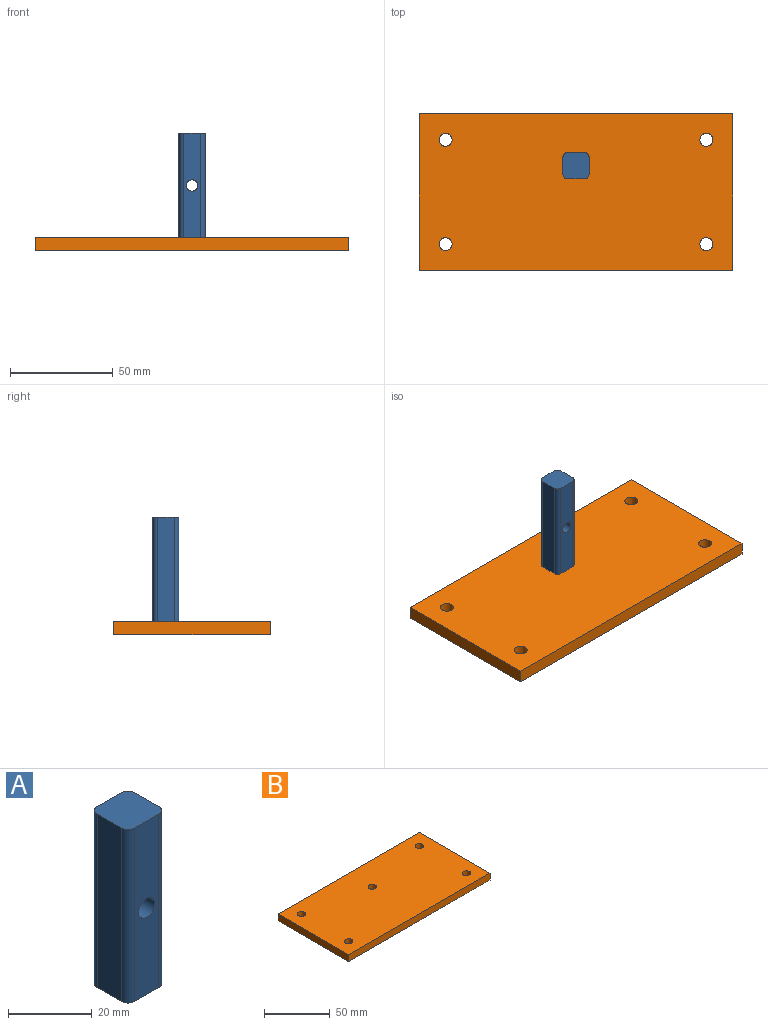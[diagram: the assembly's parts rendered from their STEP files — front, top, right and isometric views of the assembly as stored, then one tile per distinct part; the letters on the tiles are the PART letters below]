
ASSEMBLY  parts=2 mates=1
PART A: 12 faces, bbox 12.7x12.7x50.8 mm
  f0: plane 50.8x8.13mm, normal (1,0,0), area 412.9mm2, adj f1,f7,f8,f9
  f1: cylinder r=2.29mm len=50.8mm, axis (0,0,-1), area 182.4mm2, adj f0,f2,f8,f9
  f2: plane 50.8x8.13mm, normal (0,1,0), area 388.8mm2, adj f1,f3,f8,f9,f10
  f3: cylinder r=2.29mm len=50.8mm, axis (0,0,-1), area 182.4mm2, adj f2,f4,f8,f9
  f4: plane 50.8x8.13mm, normal (-1,0,0), area 412.9mm2, adj f3,f5,f8,f9
  f5: cylinder r=2.29mm len=50.8mm, axis (0,0,-1), area 182.4mm2, adj f4,f6,f8,f9
  f6: plane 50.8x8.13mm, normal (0,-1,0), area 388.8mm2, adj f5,f7,f8,f9,f10
  f7: cylinder r=2.29mm len=50.8mm, axis (0,0,-1), area 182.4mm2, adj f0,f6,f8,f9
  f8: plane 12.7x12.7mm, normal (0,0,1), area 156.8mm2, adj f0,f1,f2,f3,f4,f5,f6,f7
  f9: plane 12.7x12.7mm, normal (0,0,-1), area 132.7mm2, adj f0,f1,f2,f3,f4,f5,f6,f7
  f10: cylinder r=2.77mm len=12.7mm, axis (0,-1,0), area 190.3mm2, adj f2,f6,f11
  f11: cylinder r=2.77mm len=25.4mm, axis (0,0,-1), area 411.2mm2, adj f9,f10
PART B: 11 faces, bbox 152.4x76.2x6.4 mm
  f0: plane 152.4x6.35mm, normal (0,1,0), area 967.7mm2, adj f1,f8,f9,f10
  f1: plane 76.2x6.35mm, normal (-1,0,0), area 483.9mm2, adj f0,f2,f9,f10
  f2: plane 152.4x6.35mm, normal (0,-1,0), area 967.7mm2, adj f1,f8,f9,f10
  f3: cylinder r=3.17mm len=6.35mm, axis (0,0,-1), area 126.7mm2, adj f9,f10
  f4: cylinder r=3.17mm len=6.35mm, axis (0,0,-1), area 126.7mm2, adj f9,f10
  f5: cylinder r=3.17mm len=6.35mm, axis (0,0,-1), area 126.7mm2, adj f9,f10
  f6: cylinder r=3.17mm len=6.35mm, axis (0,0,-1), area 126.7mm2, adj f9,f10
  f7: cylinder r=3.17mm len=6.35mm, axis (0,0,-1), area 126.7mm2, adj f9,f10
  f8: plane 76.2x6.35mm, normal (1,0,0), area 483.9mm2, adj f0,f2,f9,f10
  f9: plane 152.4x76.2mm, normal (0,0,1), area 11454.5mm2, adj f0,f1,f2,f3,f4,f5,f6,f7
  f10: plane 152.4x76.2mm, normal (0,0,-1), area 11454.5mm2, adj f0,f1,f2,f3,f4,f5,f6,f7
PLACE A t=(0,50.8,6.35)mm
PLACE B at identity fixed
MATE fastened B.f7 <-> A.f11  axis (0,0,1) through (0,50.8,6.35)mm
